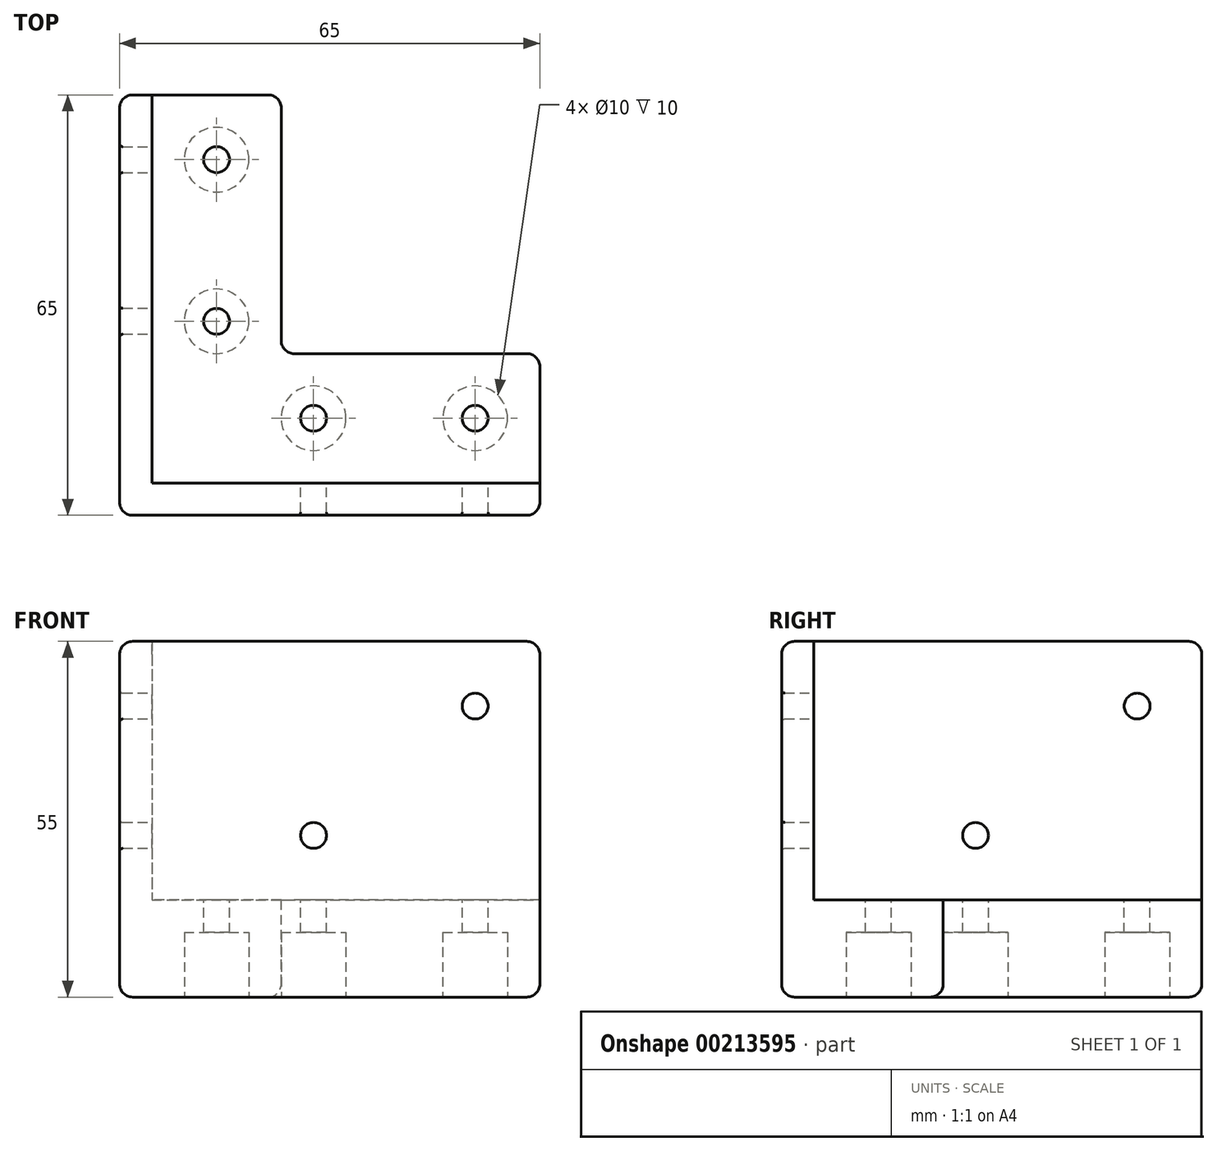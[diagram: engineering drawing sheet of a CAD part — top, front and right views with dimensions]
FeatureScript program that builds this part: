
annotation { "Feature Type Name" : "Feature", "Feature Type Description" : "" }
export const myFeature = defineFeature(function(context is Context, id is Id, definition is map)
    precondition{}
    {
        {
            var Q0;
            Q0=qCreatedBy(makeId("Top.planeOp"),FACE);
            var sketch = newSketch(context, id + "F0", { "sketchPlane" : qUnion([Q0])});
            skLineSegment(sketch, "E0", {"start": v(0, 0) * mm, "end": v(0, 40) * mm});
            skLineSegment(sketch, "E1", {"start": v(0, 40) * mm, "end": v(-25, 40) * mm});
            skLineSegment(sketch, "E2", {"start": v(-25, 40) * mm, "end": v(-25, -25) * mm});
            skLineSegment(sketch, "E3", {"start": v(-25, -25) * mm, "end": v(40, -25) * mm});
            skLineSegment(sketch, "E4", {"start": v(40, -25) * mm, "end": v(40, 0) * mm});
            skLineSegment(sketch, "E5", {"start": v(40, 0) * mm, "end": v(0, 0) * mm});
            skLineSegment(sketch, "E6", {"start": v(-20, 40) * mm, "end": v(-20, -20) * mm});
            skLineSegment(sketch, "E7", {"start": v(-20, -20) * mm, "end": v(40, -20) * mm});
            skLineSegment(sketch, "E8", {"start": v(-10, -10) * mm, "end": v(40, -10) * mm, "construction": true});
            skLineSegment(sketch, "E9", {"start": v(-10, -10) * mm, "end": v(-10, 40) * mm, "construction": true});
            skCircle(sketch, "E10", {"center": v(30, -10) * mm, "radius": 2 * mm});
            skCircle(sketch, "E11", {"center": v(5, -10) * mm, "radius": 2 * mm});
            skCircle(sketch, "E12", {"center": v(-10, 5) * mm, "radius": 2 * mm});
            skCircle(sketch, "E13", {"center": v(-10, 30) * mm, "radius": 2 * mm});
            skSolve(sketch);
        }
        {
            var Q0;
            {var subQ4=sQuery(id+"F0.wireOp",EDGE,"E0");Q0=makeQuery(id+"F0.imprint","IMPRINT",FACE,{"disambiguationData":[TD([[makeQuery(id+"F0.imprint","IMPRINT",EDGE,{"derivedFrom":subQ4}),1.0]])]});}
            var Q1;
            {var subQ3=sQuery(id+"F0.wireOp",EDGE,"E2");Q1=makeQuery(id+"F0.imprint","IMPRINT",FACE,{"disambiguationData":[TD([[makeQuery(id+"F0.imprint","IMPRINT",EDGE,{"derivedFrom":subQ3}),1.0]])]});}
            extrude(context, id + "F1", {"entities" : qUnion([Q0, Q1]), "oppositeDirection" : true, "depth" : 15 * mm});
        }
        {
            var Q0;
            {var subQ3=sQuery(id+"F0.wireOp",EDGE,"E2");Q0=makeQuery(id+"F0.imprint","IMPRINT",FACE,{"disambiguationData":[TD([[makeQuery(id+"F0.imprint","IMPRINT",EDGE,{"derivedFrom":subQ3}),1.0]])]});}
            extrude(context, id + "F2", {"entities" : qUnion([Q0]), "operationType" : NewBodyOperationType.ADD, "depth" : 40 * mm});
        }
        {
            var Q0;
            Q0=makeQuery(id+"F1.opExtrude","CAP_FACE",FACE,{"disambiguationData":[OSD([sQuery(id+"F0.wireOp",EDGE,"E0"),sQuery(id+"F0.wireOp",EDGE,"E1"),sQuery(id+"F0.wireOp",EDGE,"E2"),sQuery(id+"F0.wireOp",EDGE,"E3"),sQuery(id+"F0.wireOp",EDGE,"E4"),sQuery(id+"F0.wireOp",EDGE,"E5"),sQuery(id+"F0.wireOp",EDGE,"E10"),sQuery(id+"F0.wireOp",EDGE,"E11"),sQuery(id+"F0.wireOp",EDGE,"E12"),sQuery(id+"F0.wireOp",EDGE,"E13")])],"isStart":false});
            var sketch = newSketch(context, id + "F3", { "sketchPlane" : qUnion([Q0])});
            skCircle(sketch, "E14", {"center": v(-10, -30) * mm, "radius": 5 * mm});
            skCircle(sketch, "E15", {"center": v(-10, -5) * mm, "radius": 5 * mm});
            skCircle(sketch, "E16", {"center": v(5, 10) * mm, "radius": 5 * mm});
            skCircle(sketch, "E17", {"center": v(30, 10) * mm, "radius": 5 * mm});
            skSolve(sketch);
        }
        {
            var Q0;
            Q0=makeQuery(id+"F3.imprint","IMPRINT",FACE,{"disambiguationData":[TD([[makeQuery(id+"F3.imprint","IMPRINT",EDGE,{"derivedFrom":sQuery(id+"F3.wireOp",EDGE,"E14")}),1.0]])]});
            var Q1;
            Q1=makeQuery(id+"F3.imprint","IMPRINT",FACE,{"disambiguationData":[TD([[makeQuery(id+"F3.imprint","IMPRINT",EDGE,{"derivedFrom":sQuery(id+"F3.wireOp",EDGE,"E15")}),1.0]])]});
            var Q2;
            Q2=makeQuery(id+"F3.imprint","IMPRINT",FACE,{"disambiguationData":[TD([[makeQuery(id+"F3.imprint","IMPRINT",EDGE,{"derivedFrom":sQuery(id+"F3.wireOp",EDGE,"E16")}),1.0]])]});
            var Q3;
            Q3=makeQuery(id+"F3.imprint","IMPRINT",FACE,{"disambiguationData":[TD([[makeQuery(id+"F3.imprint","IMPRINT",EDGE,{"derivedFrom":sQuery(id+"F3.wireOp",EDGE,"E17")}),1.0]])]});
            extrude(context, id + "F4", {"entities" : qUnion([Q0, Q1, Q2, Q3]), "operationType" : NewBodyOperationType.REMOVE, "oppositeDirection" : true, "depth" : 10 * mm});
        }
        {
            var Q0;
            {var subQ0=sQuery(id+"F0.wireOp",EDGE,"E3");var subQ1=sQuery(id+"F0.wireOp",EDGE,"E2");Q0=makeQuery(id+"F2.boolean.opBoolean","MERGE",EDGE,{"derivedFrom":[makeQuery(id+"F1.opExtrude","SWEPT_EDGE",EDGE,{"disambiguationData":[OSD([subQ1,subQ0])]}),makeQuery(id+"F2.opExtrude","SWEPT_EDGE",EDGE,{"disambiguationData":[OSD([subQ1,subQ0])]})]});}
            var Q1;
            Q1=makeQuery(id+"F1.opExtrude","CAP_EDGE",EDGE,{"disambiguationData":[OSD([sQuery(id+"F0.wireOp",EDGE,"E2")])],"isStart":false});
            var Q2;
            Q2=makeQuery(id+"F1.opExtrude","CAP_EDGE",EDGE,{"disambiguationData":[OSD([sQuery(id+"F0.wireOp",EDGE,"E3")])],"isStart":false});
            var Q3;
            Q3=makeQuery(id+"F1.opExtrude","CAP_EDGE",EDGE,{"disambiguationData":[OSD([sQuery(id+"F0.wireOp",EDGE,"E5")])],"isStart":false});
            var Q4;
            Q4=makeQuery(id+"F1.opExtrude","CAP_EDGE",EDGE,{"disambiguationData":[OSD([sQuery(id+"F0.wireOp",EDGE,"E0")])],"isStart":false});
            var Q5;
            Q5=makeQuery(id+"F1.opExtrude","CAP_EDGE",EDGE,{"disambiguationData":[OSD([sQuery(id+"F0.wireOp",EDGE,"E1")])],"isStart":false});
            var Q6;
            Q6=makeQuery(id+"F1.opExtrude","CAP_EDGE",EDGE,{"disambiguationData":[OSD([sQuery(id+"F0.wireOp",EDGE,"E4")])],"isStart":false});
            var Q7;
            {var subQ0=sQuery(id+"F0.wireOp",EDGE,"E4");var subQ1=sQuery(id+"F0.wireOp",EDGE,"E3");Q7=makeQuery(id+"F2.boolean.opBoolean","MERGE",EDGE,{"derivedFrom":[makeQuery(id+"F1.opExtrude","SWEPT_EDGE",EDGE,{"disambiguationData":[OSD([subQ1,subQ0])]}),makeQuery(id+"F2.opExtrude","SWEPT_EDGE",EDGE,{"disambiguationData":[OSD([subQ1,subQ0])]})]});}
            var Q8;
            Q8=makeQuery(id+"F2.opExtrude","CAP_EDGE",EDGE,{"disambiguationData":[OSD([sQuery(id+"F0.wireOp",EDGE,"E3")])],"isStart":false});
            var Q9;
            Q9=makeQuery(id+"F2.opExtrude","CAP_EDGE",EDGE,{"disambiguationData":[OSD([sQuery(id+"F0.wireOp",EDGE,"E2")])],"isStart":false});
            var Q10;
            {var subQ0=sQuery(id+"F0.wireOp",EDGE,"E2");var subQ1=sQuery(id+"F0.wireOp",EDGE,"E1");Q10=makeQuery(id+"F2.boolean.opBoolean","MERGE",EDGE,{"derivedFrom":[makeQuery(id+"F1.opExtrude","SWEPT_EDGE",EDGE,{"disambiguationData":[OSD([subQ1,subQ0])]}),makeQuery(id+"F2.opExtrude","SWEPT_EDGE",EDGE,{"disambiguationData":[OSD([subQ1,subQ0])]})]});}
            var Q11;
            Q11=makeQuery(id+"F1.opExtrude","SWEPT_EDGE",EDGE,{"disambiguationData":[OSD([sQuery(id+"F0.wireOp",EDGE,"E4"),sQuery(id+"F0.wireOp",EDGE,"E5")])]});
            var Q12;
            Q12=makeQuery(id+"F1.opExtrude","SWEPT_EDGE",EDGE,{"disambiguationData":[OSD([sQuery(id+"F0.wireOp",EDGE,"E0"),sQuery(id+"F0.wireOp",EDGE,"E1")])]});
            var Q13;
            Q13=makeQuery(id+"F1.opExtrude","SWEPT_EDGE",EDGE,{"disambiguationData":[OSD([sQuery(id+"F0.wireOp",EDGE,"E0"),sQuery(id+"F0.wireOp",EDGE,"E5")])]});
            var Q14;
            Q14=makeQuery(id+"F2.opExtrude","CAP_EDGE",EDGE,{"disambiguationData":[OSD([sQuery(id+"F0.wireOp",EDGE,"E4")])],"isStart":false});
            var Q15;
            Q15=makeQuery(id+"F2.opExtrude","CAP_EDGE",EDGE,{"disambiguationData":[OSD([sQuery(id+"F0.wireOp",EDGE,"E1")])],"isStart":false});
            fillet(context, id + "F5", {"entities" : qUnion([Q0, Q1, Q2, Q3, Q4, Q5, Q6, Q7, Q8, Q9, Q10, Q11, Q12, Q13, Q14, Q15]), "radius" : 2 * mm, "tangentPropagation" : true, "allowEdgeOverflow" : false});
        }
        {
            var Q0;
            Q0=makeQuery(id+"F2.opExtrude","SWEPT_FACE",FACE,{"disambiguationData":[OSD([sQuery(id+"F0.wireOp",EDGE,"E7")])]});
            var sketch = newSketch(context, id + "F6", { "sketchPlane" : qUnion([Q0])});
            skCircle(sketch, "E18", {"center": v(-30, 30) * mm, "radius": 2 * mm});
            skCircle(sketch, "E19", {"center": v(-5, 10) * mm, "radius": 2 * mm});
            skSolve(sketch);
        }
        {
            var Q0;
            Q0=makeQuery(id+"F6.imprint","IMPRINT",FACE,{"disambiguationData":[TD([[makeQuery(id+"F6.imprint","IMPRINT",EDGE,{"derivedFrom":sQuery(id+"F6.wireOp",EDGE,"E18")}),1.0]])]});
            var Q1;
            Q1=makeQuery(id+"F6.imprint","IMPRINT",FACE,{"disambiguationData":[TD([[makeQuery(id+"F6.imprint","IMPRINT",EDGE,{"derivedFrom":sQuery(id+"F6.wireOp",EDGE,"E19")}),1.0]])]});
            extrude(context, id + "F7", {"entities" : qUnion([Q0, Q1]), "operationType" : NewBodyOperationType.REMOVE, "oppositeDirection" : true, "depth" : 25 * mm});
        }
        {
            var Q0;
            Q0=makeQuery(id+"F2.opExtrude","SWEPT_FACE",FACE,{"disambiguationData":[OSD([sQuery(id+"F0.wireOp",EDGE,"E6")])]});
            var sketch = newSketch(context, id + "F8", { "sketchPlane" : qUnion([Q0])});
            skCircle(sketch, "E20", {"center": v(30, 30) * mm, "radius": 2 * mm});
            skCircle(sketch, "E21", {"center": v(5, 10) * mm, "radius": 2 * mm});
            skSolve(sketch);
        }
        {
            var Q0;
            Q0=makeQuery(id+"F8.imprint","IMPRINT",FACE,{"disambiguationData":[TD([[makeQuery(id+"F8.imprint","IMPRINT",EDGE,{"derivedFrom":sQuery(id+"F8.wireOp",EDGE,"E20")}),1.0]])]});
            var Q1;
            Q1=makeQuery(id+"F8.imprint","IMPRINT",FACE,{"disambiguationData":[TD([[makeQuery(id+"F8.imprint","IMPRINT",EDGE,{"derivedFrom":sQuery(id+"F8.wireOp",EDGE,"E21")}),1.0]])]});
            extrude(context, id + "F9", {"entities" : qUnion([Q0, Q1]), "operationType" : NewBodyOperationType.REMOVE, "oppositeDirection" : true, "depth" : 25 * mm});
        }
        {
            var Q0;
            {var subQ0=sQuery(id+"F0.wireOp",EDGE,"E2");Q0=makeQuery(id+"F9.boolean.opBoolean","INTERSECT",EDGE,{"derivedFrom":[makeQuery(id+"F2.boolean.opBoolean","MERGE",FACE,{"derivedFrom":[makeQuery(id+"F1.opExtrude","SWEPT_FACE",FACE,{"disambiguationData":[OSD([subQ0])]}),makeQuery(id+"F2.opExtrude","SWEPT_FACE",FACE,{"disambiguationData":[OSD([subQ0])]})]}),makeQuery(id+"F9.opExtrude","SWEPT_FACE",FACE,{"disambiguationData":[OSD([sQuery(id+"F8.wireOp",EDGE,"E21")])]})]});}
            var Q1;
            {var subQ0=sQuery(id+"F0.wireOp",EDGE,"E2");Q1=makeQuery(id+"F9.boolean.opBoolean","INTERSECT",EDGE,{"derivedFrom":[makeQuery(id+"F2.boolean.opBoolean","MERGE",FACE,{"derivedFrom":[makeQuery(id+"F1.opExtrude","SWEPT_FACE",FACE,{"disambiguationData":[OSD([subQ0])]}),makeQuery(id+"F2.opExtrude","SWEPT_FACE",FACE,{"disambiguationData":[OSD([subQ0])]})]}),makeQuery(id+"F9.opExtrude","SWEPT_FACE",FACE,{"disambiguationData":[OSD([sQuery(id+"F8.wireOp",EDGE,"E20")])]})]});}
            var Q2;
            {var subQ0=sQuery(id+"F0.wireOp",EDGE,"E3");Q2=makeQuery(id+"F7.boolean.opBoolean","INTERSECT",EDGE,{"derivedFrom":[makeQuery(id+"F2.boolean.opBoolean","MERGE",FACE,{"derivedFrom":[makeQuery(id+"F1.opExtrude","SWEPT_FACE",FACE,{"disambiguationData":[OSD([subQ0])]}),makeQuery(id+"F2.opExtrude","SWEPT_FACE",FACE,{"disambiguationData":[OSD([subQ0])]})]}),makeQuery(id+"F7.opExtrude","SWEPT_FACE",FACE,{"disambiguationData":[OSD([sQuery(id+"F6.wireOp",EDGE,"E19")])]})]});}
            var Q3;
            {var subQ0=sQuery(id+"F0.wireOp",EDGE,"E3");Q3=makeQuery(id+"F7.boolean.opBoolean","INTERSECT",EDGE,{"derivedFrom":[makeQuery(id+"F2.boolean.opBoolean","MERGE",FACE,{"derivedFrom":[makeQuery(id+"F1.opExtrude","SWEPT_FACE",FACE,{"disambiguationData":[OSD([subQ0])]}),makeQuery(id+"F2.opExtrude","SWEPT_FACE",FACE,{"disambiguationData":[OSD([subQ0])]})]}),makeQuery(id+"F7.opExtrude","SWEPT_FACE",FACE,{"disambiguationData":[OSD([sQuery(id+"F6.wireOp",EDGE,"E18")])]})]});}
            fillet(context, id + "F10", {"entities" : qUnion([Q0, Q1, Q2, Q3]), "radius" : 0.5 * mm, "tangentPropagation" : true, "allowEdgeOverflow" : false});
        }
    });
